# Revit family: Fitting-Ninety_Degree_Angle-Unistrut-P1130-P1131
name_source: partatom
category: Specialty Equipment
revit_build: Autodesk Revit MEP 2012 (Build: 20110309_2315(x64)
units: mm (PartAtom-declared; Revit-internal decimal feet)

## types (2) — shared parameters
04 CSI = 26 05 48
95 CSI = 16070
Assembly Code = D5020100
CAD URL = http://unistrut.us
Hole Diameter = 9/16"
Literature URL = http://unistrut.us
Load Capacity Note = Visit the product page for load application and capacity.
Manufacturer = Unistrut by Atkore International
Manufacturer Fax = 708-339-7814
Overall Height = 3 3/4"
Overall Length = 1 7/8"
Part Type = Fitting
Power Strut Part Number = PS 689
Product Page URL = http://unistrut.us
Subcategory = Nintey Degree Angle Fittings
Thickness = 1/4"
URL = http://unistrut.us
Unistrut Part Number = P1130
Unit = <By Category>
ecoScorecard Product Page = http://products.ecoscorecard.com
ecoScorecard_data = http://products.ecoscorecard.com

## per-type parameters (varying)
| type | Default Elevation | Overall Width | Weight Per Piece |
| P1130 | 48" | 6 5/8" | 1.90 lb |
| P1131 | 0" | 8 5/8" | 2.42 lb |

note: column(s) folded — value = type name in every type: Model

## geometry (parser evidence)
native form markers: Sweep x4
no freeform markers — native parametric forms only
